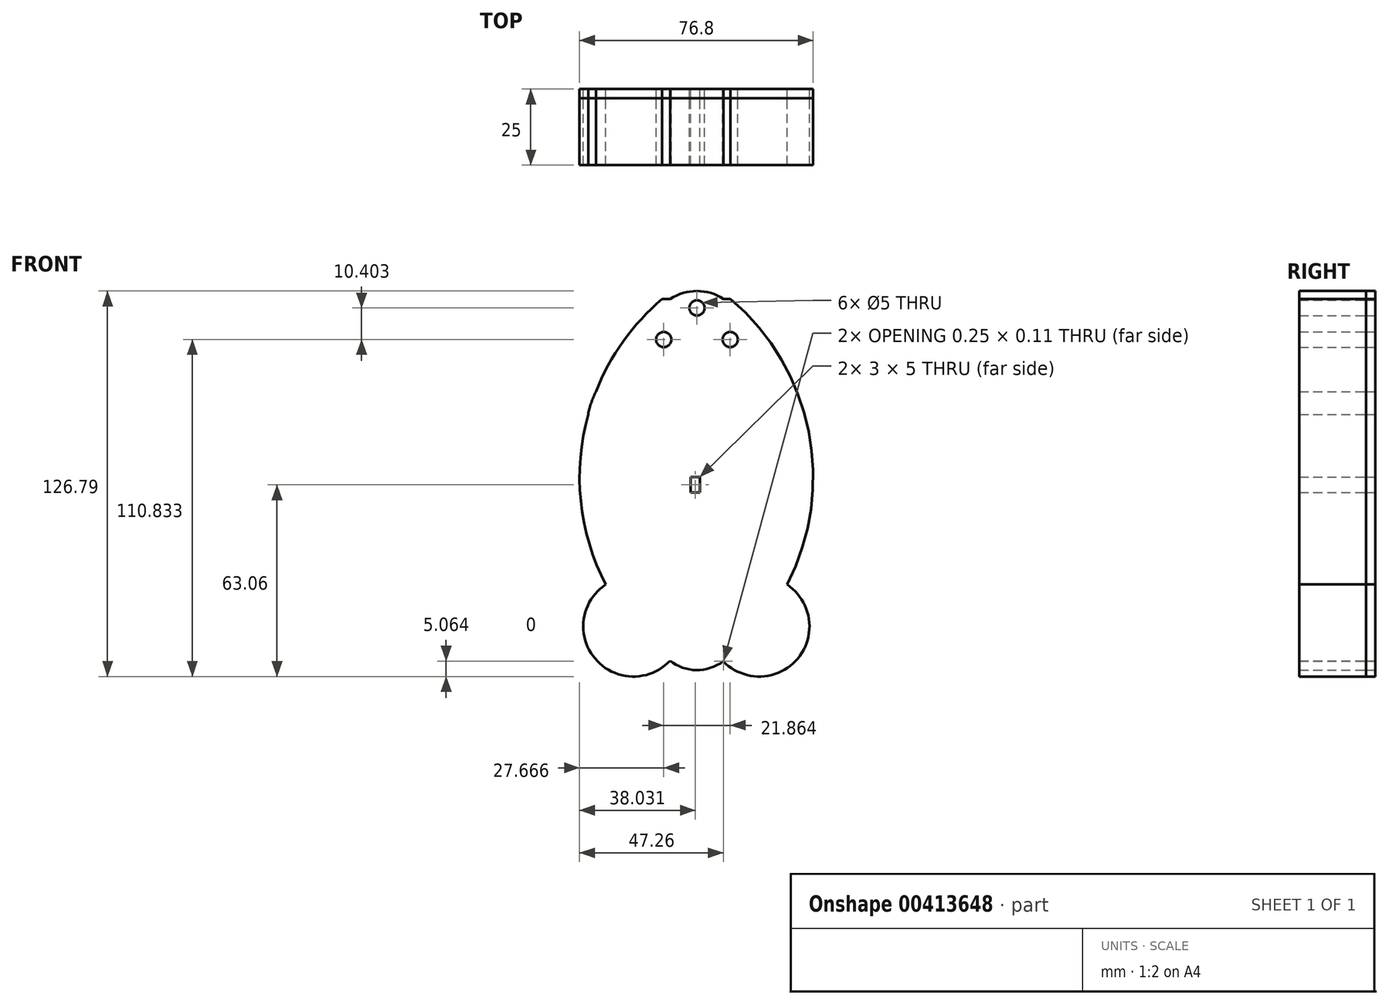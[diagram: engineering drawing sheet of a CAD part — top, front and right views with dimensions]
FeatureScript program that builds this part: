
annotation { "Feature Type Name" : "Feature", "Feature Type Description" : "" }
export const myFeature = defineFeature(function(context is Context, id is Id, definition is map)
    precondition{}
    {
        {
            var Q0;
            Q0=qCreatedBy(makeId("Front.planeOp"),FACE);
            var sketch = newSketch(context, id + "F0", { "sketchPlane" : qUnion([Q0])});
            skArc(sketch, "E0", {"start": v(8.48, -60.68) * mm, "mid": v(8.75, -60.47) * mm, "end": v(9.02, -60.26) * mm});
            skArc(sketch, "E1", {"start": v(-11.42, 58.62) * mm, "mid": v(-24.23, 44.73) * mm, "end": v(-33.26, 28.13) * mm});
            skArc(sketch, "E2", {"start": v(8.76, 58.62) * mm, "mid": v(0, 61.23) * mm, "end": v(-8.76, 58.62) * mm});
            skLineSegment(sketch, "E3", {"start": v(8.76, 58.62) * mm, "end": v(11.03, 58.62) * mm});
            skLineSegment(sketch, "E4", {"start": v(11.03, 58.62) * mm, "end": v(8.76, 58.62) * mm});
            skPoint(sketch, "E5.start.orphan", {"position": v(0, 61.23) * mm});
            skLineSegment(sketch, "E6.trimOffspring", {"start": v(-8.76, 58.62) * mm, "end": v(-11.42, 58.62) * mm});
            skCircle(sketch, "E7", {"center": v(20.49, -49.06) * mm, "radius": 16.5 * mm});
            skCircle(sketch, "E8", {"center": v(-20.88, -49.06) * mm, "radius": 16.5 * mm});
            skArc(sketch, "E9.trimOffspring", {"start": v(29.6, -35.31) * mm, "mid": v(36.74, 14.9) * mm, "end": v(11.03, 58.62) * mm});
            skPoint(sketch, "E10.orphan", {"position": v(0, -49.06) * mm});
            skArc(sketch, "E11", {"start": v(-33.26, 28.13) * mm, "mid": v(-34.76, 24.47) * mm, "end": v(-35.77, 20.65) * mm});
            skPoint(sketch, "E12.orphan", {"position": v(0, 35.57) * mm});
            skLineSegment(sketch, "E13", {"start": v(-28.59, -5.03) * mm, "end": v(-28.69, -5.03) * mm});
            skPoint(sketch, "E13.endSnap0", {"position": v(-36.03, 10.79) * mm});
            skPoint(sketch, "E14.orphan", {"position": v(-36.03, -5.03) * mm});
            skLineSegment(sketch, "E15.trimOffspring", {"start": v(-30.9, 32.14) * mm, "end": v(-31.55, 32.14) * mm});
            skArc(sketch, "E16.trimOffspring", {"start": v(-9.26, -60.38) * mm, "mid": v(-9.15, -60.47) * mm, "end": v(-9.04, -60.55) * mm});
            skPoint(sketch, "E17.trimOffspring.end.orphan", {"position": v(-44.78, -60.26) * mm});
            skLineSegment(sketch, "E18.trimOffspring", {"start": v(-8.87, -60.38) * mm, "end": v(-9.26, -60.38) * mm});
            skLineSegment(sketch, "E19.trimOffspring", {"start": v(8.78, -60.44) * mm, "end": v(8.54, -60.44) * mm});
            skPoint(sketch, "E20.orphan", {"position": v(0, 14.94) * mm});
            skPoint(sketch, "E21.center.orphan", {"position": v(0, -43.25) * mm});
            skPoint(sketch, "E21.start.orphan", {"position": v(9.02, -60.26) * mm});
            skArc(sketch, "E22.trimOffspring", {"start": v(-35.77, 20.65) * mm, "mid": v(-38.2, -7.88) * mm, "end": v(-30, -35.31) * mm});
            skPoint(sketch, "E23.center.orphan", {"position": v(19.99, 0) * mm});
            skPoint(sketch, "E24.center.orphan", {"position": v(-21.59, 0) * mm});
            skLineSegment(sketch, "E25", {"start": v(0, 45.27) * mm, "end": v(10.93, 45.27) * mm});
            skLineSegment(sketch, "E26", {"start": v(0, 45.27) * mm, "end": v(-10.93, 45.27) * mm});
            skCircle(sketch, "E27", {"center": v(10.93, 45.27) * mm, "radius": 2.5 * mm});
            skCircle(sketch, "E28", {"center": v(-10.93, 45.27) * mm, "radius": 2.5 * mm});
            skArc(sketch, "E29", {"start": v(-8.87, -60.38) * mm, "mid": v(-0.14, -63.44) * mm, "end": v(8.65, -60.56) * mm});
            skPoint(sketch, "E30.center.orphan", {"position": v(0, 55.68) * mm});
            skCircle(sketch, "E31", {"center": v(0, 55.68) * mm, "radius": 2.5 * mm});
            skLineSegment(sketch, "E32", {"start": v(-2.07, 0) * mm, "end": v(0.93, 0) * mm});
            skPoint(sketch, "E33.end.orphan", {"position": v(0, 6.74) * mm});
            skLineSegment(sketch, "E34", {"start": v(-2.07, 0) * mm, "end": v(-2.07, -5) * mm});
            skLineSegment(sketch, "E35", {"start": v(0.93, 0) * mm, "end": v(0.93, -5) * mm});
            skLineSegment(sketch, "E36", {"start": v(0.93, -5) * mm, "end": v(-2.07, -5) * mm});
            skSolve(sketch);
        }
        {
            var Q0;
            Q0 = qSketchRegion(id + "F0", true);
            extrude(context, id + "F1", {"entities" : qUnion([Q0]), "depth" : 25 * mm});
        }
        {
            var Q0;
            Q0 = qSketchRegion(id + "F0", true);
            extrude(context, id + "F2", {"entities" : qUnion([Q0]), "depth" : 3 * mm});
        }
    });
